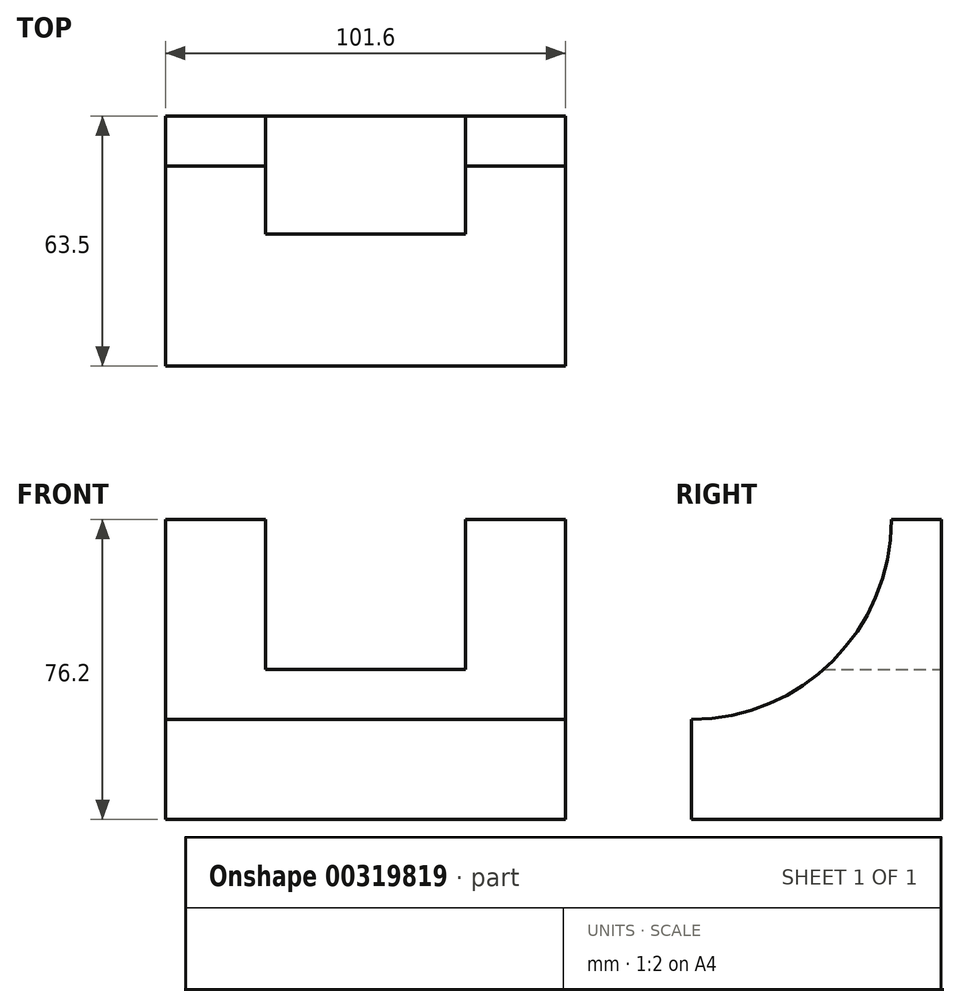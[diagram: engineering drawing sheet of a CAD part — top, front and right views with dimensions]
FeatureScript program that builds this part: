
annotation { "Feature Type Name" : "Feature", "Feature Type Description" : "" }
export const myFeature = defineFeature(function(context is Context, id is Id, definition is map)
    precondition{}
    {
        {
            var Q0;
            Q0=qCreatedBy(makeId("Front.planeOp"),FACE);
            var sketch = newSketch(context, id + "F0", { "sketchPlane" : qUnion([Q0])});
            skLineSegment(sketch, "E0.bottom", {"start": v(-45.7, 38.44) * mm, "end": v(55.9, 38.44) * mm});
            skLineSegment(sketch, "E0.top", {"start": v(-45.7, -37.76) * mm, "end": v(55.9, -37.76) * mm});
            skLineSegment(sketch, "E0.left", {"start": v(-45.7, 38.44) * mm, "end": v(-45.7, -37.76) * mm});
            skLineSegment(sketch, "E0.right", {"start": v(55.9, 38.44) * mm, "end": v(55.9, -37.76) * mm});
            skSolve(sketch);
        }
        {
            var Q0;
            Q0=makeQuery(id+"F0.imprint","IMPRINT",FACE,{"disambiguationData":[TD([[makeQuery(id+"F0.imprint","IMPRINT",EDGE,{"derivedFrom":sQuery(id+"F0.wireOp",EDGE,"E0.bottom")}),-1.0]])]});
            extrude(context, id + "F1", {"entities" : qUnion([Q0]), "depth" : 63.5 * mm});
        }
        {
            var Q0;
            Q0=makeQuery(id+"F1.opExtrude","SWEPT_FACE",FACE,{"disambiguationData":[OSD([sQuery(id+"F0.wireOp",EDGE,"E0.left")])]});
            var sketch = newSketch(context, id + "F2", { "sketchPlane" : qUnion([Q0])});
            skLineSegment(sketch, "E1", {"start": v(63.5, -37.76) * mm, "end": v(63.5, -12.36) * mm});
            skLineSegment(sketch, "E2", {"start": v(0, 38.44) * mm, "end": v(12.7, 38.44) * mm});
            skArc(sketch, "E3", {"start": v(12.7, 38.44) * mm, "mid": v(27.6, 2.54) * mm, "end": v(63.5, -12.36) * mm});
            skSolve(sketch);
        }
        {
            var Q0;
            {var subQ0=sQuery(id+"F2.wireOp",EDGE,"E3");Q0=makeQuery(id+"F2.imprint","IMPRINT",FACE,{"disambiguationData":[TD([[makeQuery(id+"F2.imprint","IMPRINT",EDGE,{"derivedFrom":subQ0}),1.0]])]});}
            extrude(context, id + "F3", {"entities" : qUnion([Q0]), "operationType" : NewBodyOperationType.REMOVE, "oppositeDirection" : true, "depth" : 127 * mm});
        }
        {
            var Q0;
            Q0=makeQuery(id+"F1.opExtrude","CAP_FACE",FACE,{"disambiguationData":[OSD([sQuery(id+"F0.wireOp",EDGE,"E0.bottom"),sQuery(id+"F0.wireOp",EDGE,"E0.top"),sQuery(id+"F0.wireOp",EDGE,"E0.left"),sQuery(id+"F0.wireOp",EDGE,"E0.right")])],"isStart":true});
            var sketch = newSketch(context, id + "F4", { "sketchPlane" : qUnion([Q0])});
            skLineSegment(sketch, "E4", {"start": v(-55.9, 38.44) * mm, "end": v(-30.5, 38.44) * mm});
            skLineSegment(sketch, "E5", {"start": v(45.7, 38.44) * mm, "end": v(20.3, 38.44) * mm});
            skLineSegment(sketch, "E6", {"start": v(-30.5, 38.44) * mm, "end": v(20.3, 38.44) * mm});
            skLineSegment(sketch, "E7", {"start": v(20.3, 0.34) * mm, "end": v(-30.5, 0.34) * mm});
            skLineSegment(sketch, "E8", {"start": v(-30.5, 0.34) * mm, "end": v(-30.5, 38.44) * mm});
            skLineSegment(sketch, "E9", {"start": v(20.3, 0.34) * mm, "end": v(20.3, 38.44) * mm});
            skSolve(sketch);
        }
        {
            var Q0;
            Q0=makeQuery(id+"F4.imprint","IMPRINT",FACE,{"disambiguationData":[TD([[makeQuery(id+"F4.imprint","IMPRINT",EDGE,{"derivedFrom":sQuery(id+"F4.wireOp",EDGE,"E6")}),1.0]])]});
            extrude(context, id + "F5", {"entities" : qUnion([Q0]), "operationType" : NewBodyOperationType.REMOVE, "oppositeDirection" : true, "depth" : 57.15 * mm});
        }
    });
